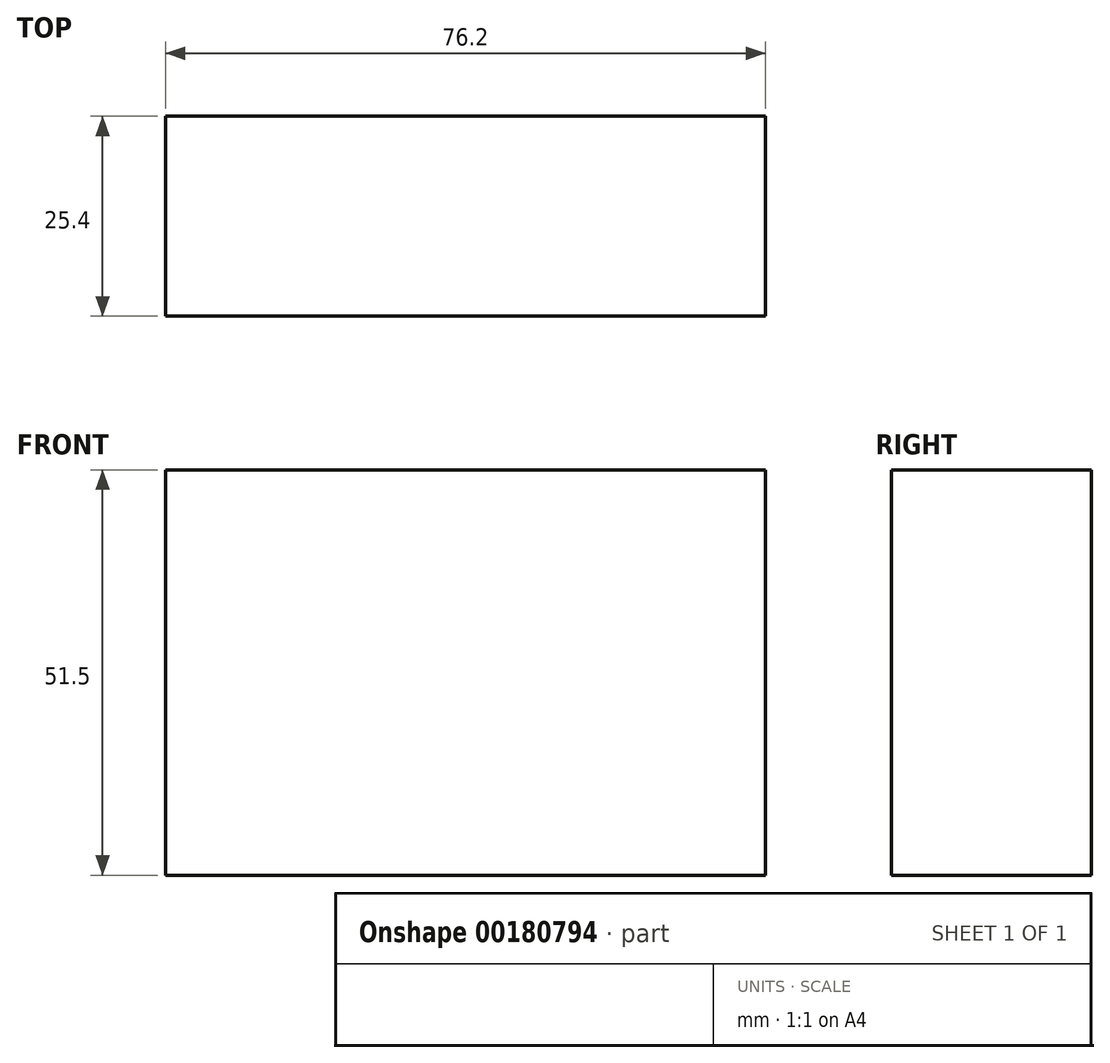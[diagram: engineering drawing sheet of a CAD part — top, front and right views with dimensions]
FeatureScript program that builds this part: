
annotation { "Feature Type Name" : "Feature", "Feature Type Description" : "" }
export const myFeature = defineFeature(function(context is Context, id is Id, definition is map)
    precondition{}
    {
        {
            var Q0;
            Q0=qCreatedBy(makeId("Front.planeOp"),FACE);
            var sketch = newSketch(context, id + "F0", { "sketchPlane" : qUnion([Q0])});
            skLineSegment(sketch, "E0.bottom", {"start": v(38.1, 25.75) * mm, "end": v(-38.1, 25.75) * mm});
            skLineSegment(sketch, "E0.top", {"start": v(38.1, -25.75) * mm, "end": v(-38.1, -25.75) * mm});
            skLineSegment(sketch, "E0.left", {"start": v(38.1, 25.75) * mm, "end": v(38.1, -25.75) * mm});
            skLineSegment(sketch, "E0.right", {"start": v(-38.1, 25.75) * mm, "end": v(-38.1, -25.75) * mm});
            skPoint(sketch, "E0.middle", {"position": v(0, 0) * mm});
            skSolve(sketch);
        }
        {
            var Q0;
            Q0=qCreatedBy(makeId("Front.planeOp"),FACE);
            var sketch = newSketch(context, id + "F1", { "sketchPlane" : qUnion([Q0])});
            skCircle(sketch, "E1", {"center": v(0, 0) * mm, "radius": 12.7 * mm});
            skSolve(sketch);
        }
        {
            var Q0;
            Q0=sQuery(id+"F1.wireOp",EDGE,"E1");
            extrude(context, id + "F2", {"bodyType" : ToolBodyType.SURFACE, "surfaceEntities" : qUnion([Q0]), "depth" : 101.6 * mm});
        }
        {
            var Q0;
            Q0=makeQuery(id+"F0.imprint","IMPRINT",FACE,{"disambiguationData":[TD([[makeQuery(id+"F0.imprint","IMPRINT",EDGE,{"derivedFrom":sQuery(id+"F0.wireOp",EDGE,"E0.bottom")}),1.0]])]});
            extrude(context, id + "F3", {"entities" : qUnion([Q0]), "oppositeDirection" : true, "depth" : 25.4 * mm});
        }
    });
